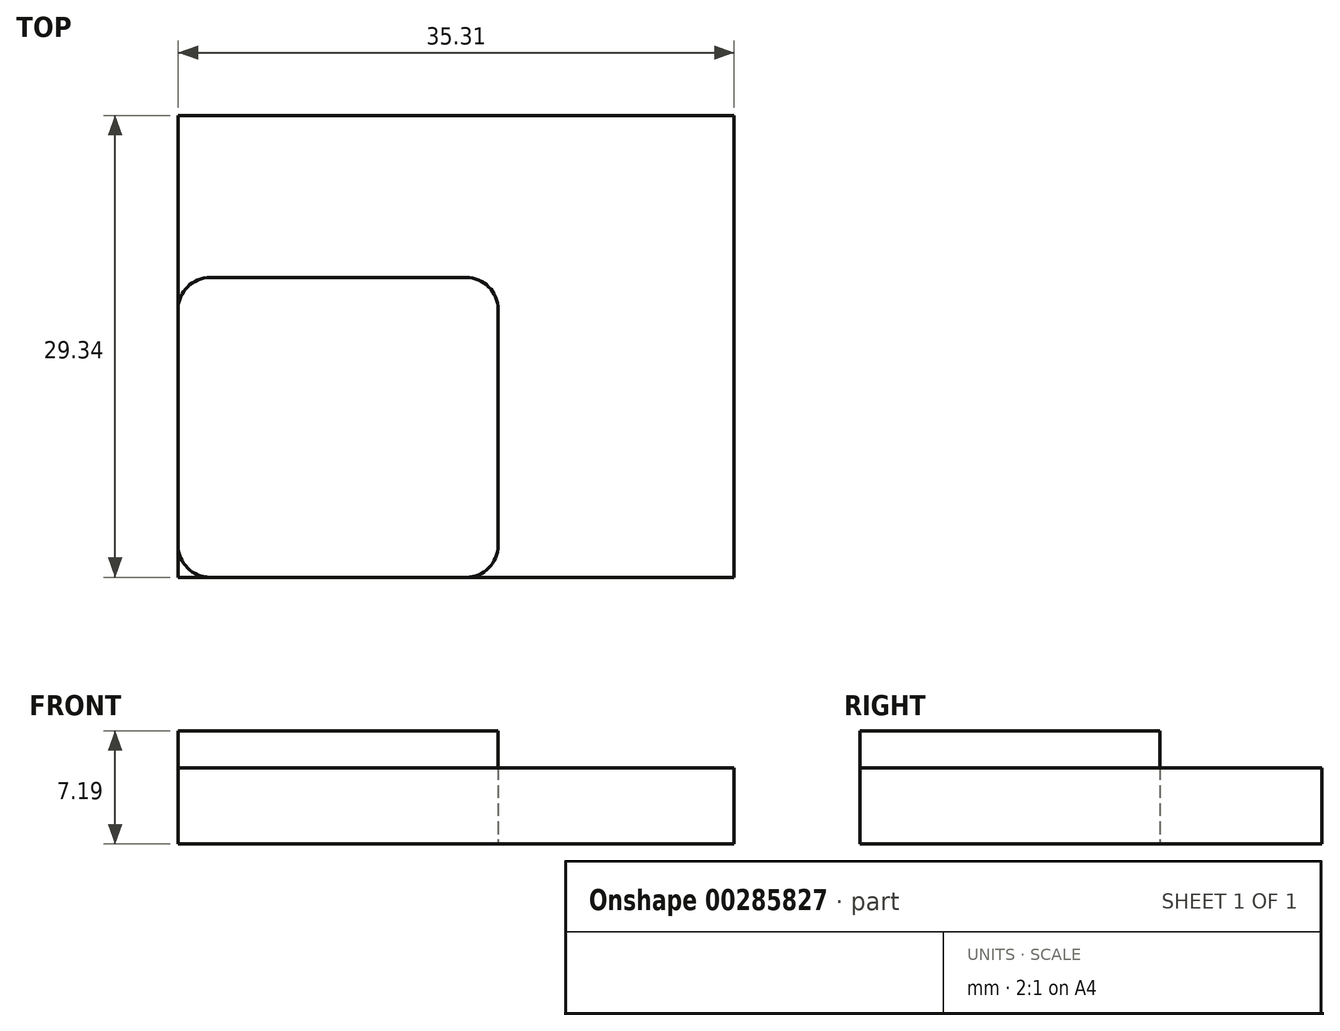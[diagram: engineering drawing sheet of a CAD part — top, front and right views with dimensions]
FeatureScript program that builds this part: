
annotation { "Feature Type Name" : "Feature", "Feature Type Description" : "" }
export const myFeature = defineFeature(function(context is Context, id is Id, definition is map)
    precondition{}
    {
        {
            var Q0;
            Q0=qCreatedBy(makeId("Top.planeOp"),FACE);
            var sketch = newSketch(context, id + "F0", { "sketchPlane" : qUnion([Q0])});
            skLineSegment(sketch, "E0.bottom", {"start": v(0, 0) * mm, "end": v(35.3, 0) * mm});
            skLineSegment(sketch, "E0.top", {"start": v(0, 29.34) * mm, "end": v(35.3, 29.34) * mm});
            skLineSegment(sketch, "E0.left", {"start": v(0, 0) * mm, "end": v(0, 29.34) * mm});
            skLineSegment(sketch, "E0.right", {"start": v(35.3, 0) * mm, "end": v(35.3, 29.34) * mm});
            skSolve(sketch);
        }
        {
            var Q0;
            Q0=makeQuery(id+"F0.imprint","IMPRINT",FACE,{"disambiguationData":[TD([[makeQuery(id+"F0.imprint","IMPRINT",EDGE,{"derivedFrom":sQuery(id+"F0.wireOp",EDGE,"E0.bottom")}),1.0]])]});
            extrude(context, id + "F1", {"entities" : qUnion([Q0]), "depth" : 4.83 * mm});
        }
        {
            var Q0;
            Q0=qCreatedBy(makeId("Top.planeOp"),FACE);
            var sketch = newSketch(context, id + "F2", { "sketchPlane" : qUnion([Q0])});
            skLineSegment(sketch, "E1.bottom", {"start": v(2.03, 0) * mm, "end": v(18.29, 0) * mm});
            skLineSegment(sketch, "E1.top", {"start": v(2.03, 19.05) * mm, "end": v(18.29, 19.05) * mm});
            skLineSegment(sketch, "E1.left", {"start": v(0, 2.03) * mm, "end": v(0, 17.02) * mm});
            skLineSegment(sketch, "E1.right", {"start": v(20.32, 2.03) * mm, "end": v(20.32, 17.02) * mm});
            skPoint(sketch, "E2.visualSharp", {"position": v(0, 19.05) * mm});
            skArc(sketch, "E2.filletArc", {"start": v(2.03, 19.05) * mm, "mid": v(0.6, 18.45) * mm, "end": v(0, 17.02) * mm});
            skPoint(sketch, "E3.visualSharp", {"position": v(20.32, 19.05) * mm});
            skArc(sketch, "E3.filletArc", {"start": v(20.32, 17.02) * mm, "mid": v(19.72, 18.45) * mm, "end": v(18.29, 19.05) * mm});
            skPoint(sketch, "E4.visualSharp", {"position": v(20.32, 0) * mm});
            skArc(sketch, "E4.filletArc", {"start": v(18.29, 0) * mm, "mid": v(19.72, 0.6) * mm, "end": v(20.32, 2.03) * mm});
            skPoint(sketch, "E5.visualSharp", {"position": v(0, 0) * mm});
            skArc(sketch, "E5.filletArc", {"start": v(0, 2.03) * mm, "mid": v(0.6, 0.6) * mm, "end": v(2.03, 0) * mm});
            skSolve(sketch);
        }
        {
            var Q0;
            Q0=makeQuery(id+"F2.imprint","IMPRINT",FACE,{"disambiguationData":[TD([[makeQuery(id+"F2.imprint","IMPRINT",EDGE,{"derivedFrom":sQuery(id+"F2.wireOp",EDGE,"E1.bottom")}),1.0]])]});
            extrude(context, id + "F3", {"entities" : qUnion([Q0]), "depth" : 7.2 * mm});
        }
    });
